# Revit family: Sanitary_Showers_hansgrohe_26858CHN-Rainfinity-Wall-outlet-Porter-5_NEW
name_source: partatom
category: Plumbing Fixtures
revit_build: Autodesk Revit 2018 (Build: 20170223_1515(x64)
units: mm (PartAtom-declared; Revit-internal decimal feet)

## family parameters
Always vertical = No
Cut with Voids When Loaded = No
OmniClass Number = 23.31.17.00
OmniClass Title = Showers
Part Type = Normal
Room Calculation Point = No
Round Connector Dimension = Use Diameter
Shared = No
Work Plane-Based = Yes

## types (4) — shared parameters
Always visible = Yes
BIMobject category = Showers
Connector Description = Water Inlet 12.7mm
Default Elevation = 1219.2 mm  [stored 4 ft]
Description = Rainfinity Wall outlet Porter 500 with shower holder and shower shelf R
Design country = Germany
Diameter = 13 mm
EAN code = 4059625229743
Edition number = 1
IFC Classification = Sanitary Terminal
Manufacturer = Hansgrohe
Manufacturer country = Germany
Manufacturer name = hansgrohe
Masterformat 2014 Code = 22 41 23
Masterformat 2014 Description = Residential Showers
Material 1 = Hansgrohe - Plastic - Graphite
Model = 26858CHN
OmniClass Code = 23-31 17 00
OmniClass Description = Showers
Outlet Connector Description = Water Outlet 12.7mm
Outlet Diameter = 13 mm
Product Guid = a4d2322c-3792-4014-bed0-1834c37e6939
Product SKU = 26858CHN
Product data url = https://bimobject.com
Product family = Rainfinity
Product group = Wall outlet
Product name = 26858CHN Rainfinity Wall outlet Porter 500 with shower holder and shower shelf R
Product url = https://pro.hansgrohe.com
QR code = https://bimobject.com
UNSPSC Code = 30181503
Uniclass 2015 Code = Pr_40_20_87_76
Uniclass 2015 Name = Shower heads
Uniformat II Code = D2010
Uniformat II Description = Plumbing Fixtures
Weight Net (Kg) = 2

## per-type parameters (varying)
| type | Material 2 | URL |
| 997 Polished Gold Optic | Hansgrohe - Metal - 997 Polished Gold Optic | https://www.hansgrohe.com |
| 677 Matt Black | Hansgrohe - Metal - 677 Matte Black | https://www.hansgrohe.com |
| 347 Brushed Black Chrome | Hansgrohe - Metal - 347 Brushed Black Chrome | https://www.hansgrohe.com |
| 147 Brushed Bronze | Hansgrohe - Metal - 147 Brushed Bronze | https://www.hansgrohe.com
https://www.hansgrohe.com |

note: [stored X ft] marks values corroborated as IEEE doubles in the binary element streams (Revit-internal decimal feet)

## geometry (parser evidence)
native form markers: Sweep x2
no freeform markers — native parametric forms only
